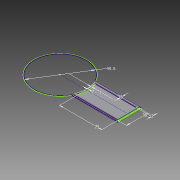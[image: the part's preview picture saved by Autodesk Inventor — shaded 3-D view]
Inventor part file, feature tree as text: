
AUTODESK INVENTOR PART (.ipt)
format: ipt  version: 2013 SP2 (Build 170200200, 200)  size: 95,744 bytes
history: native  units: mm
features: extrude x2, sketch x1
ambient origin geometry x8: Origin, YZ Plane, XZ Plane, XY Plane, X Axis, Y Axis, Z Axis, Center Point
feature tree (3):
  sketch  "Sketch1"  dims[d0=91.5mm d2=1.0mm d3=75.0mm d4=38.0mm d5=2.0mm d59=2.0mm d60=0.0mm d62=2.0mm d63=2.0mm d64=2.0mm d65=0.0mm]
  extrude  "Extrusion13"  Depth=1.0mm
  extrude  "Extrusion14"  Depth=75.0mm
